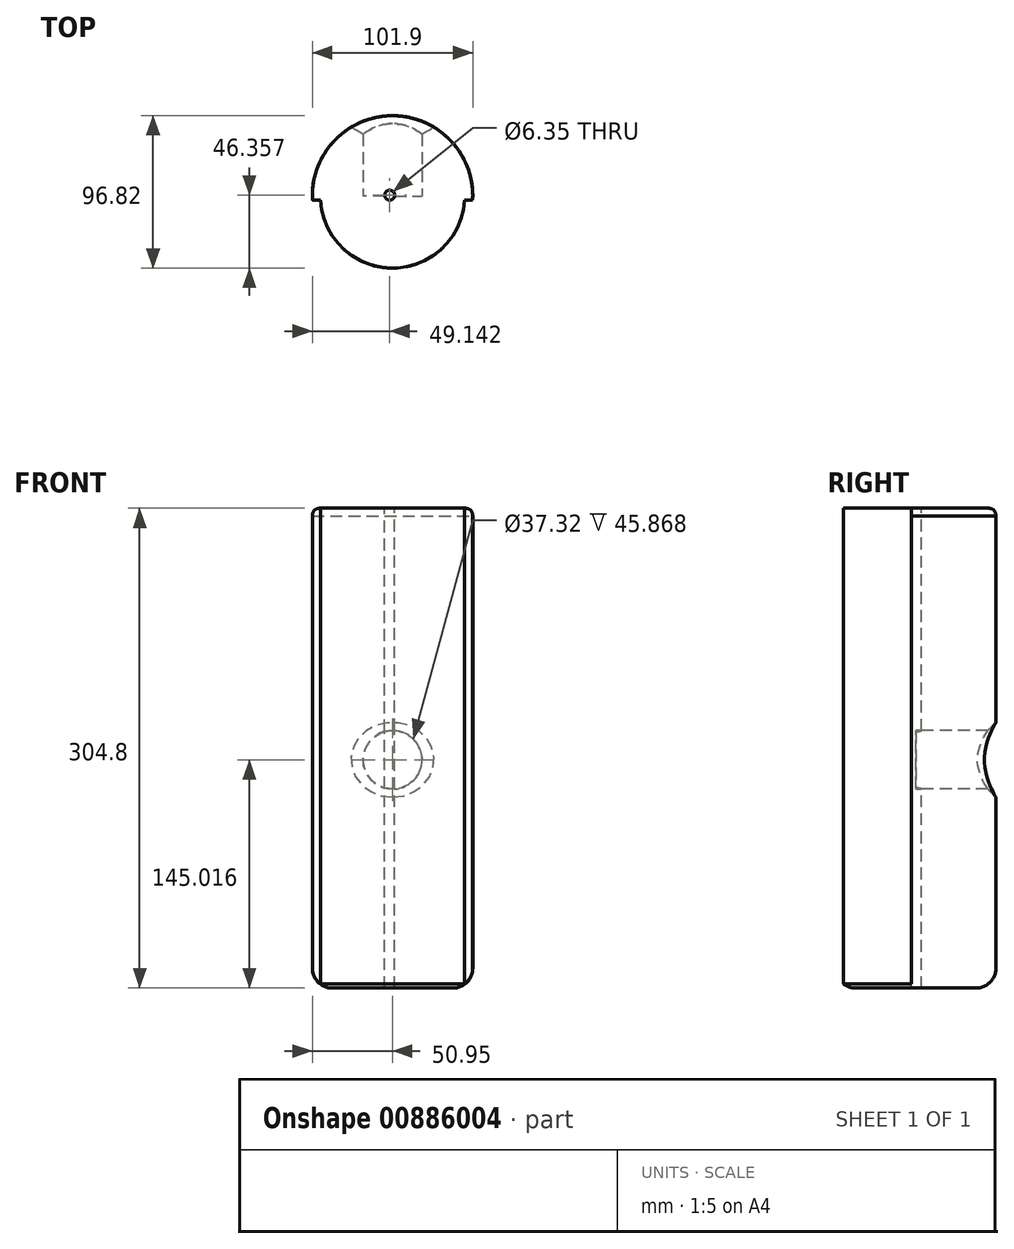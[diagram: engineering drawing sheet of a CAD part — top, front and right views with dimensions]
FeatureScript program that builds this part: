
annotation { "Feature Type Name" : "Feature", "Feature Type Description" : "" }
export const myFeature = defineFeature(function(context is Context, id is Id, definition is map)
    precondition{}
    {
        {
            var Q0;
            Q0=qCreatedBy(makeId("Top.planeOp"),FACE);
            var sketch = newSketch(context, id + "F0", { "sketchPlane" : qUnion([Q0])});
            skCircle(sketch, "E0", {"center": v(0, 0) * mm, "radius": 50.95 * mm});
            skSolve(sketch);
        }
        {
            var Q0;
            Q0 = qSketchRegion(id + "F0", true);
            extrude(context, id + "F1", {"entities" : qUnion([Q0]), "depth" : 304.8 * mm, "offsetDistance" : 25.4 * mm});
        }
        {
            var Q0;
            Q0=qCreatedBy(makeId("Front.planeOp"),FACE);
            var sketch = newSketch(context, id + "F2", { "sketchPlane" : qUnion([Q0])});
            skCircle(sketch, "E1", {"center": v(0, 145.02) * mm, "radius": 18.66 * mm});
            skSolve(sketch);
        }
        {
            var Q0;
            Q0 = qSketchRegion(id + "F2", true);
            extrude(context, id + "F3", {"entities" : qUnion([Q0]), "operationType" : NewBodyOperationType.REMOVE, "endBound" : BoundingType.THROUGH_ALL, "oppositeDirection" : true, "depth" : 25.4 * mm, "offsetDistance" : 25.4 * mm});
        }
        {
            var Q0;
            Q0=makeQuery(id+"F1.opExtrude","CAP_EDGE",EDGE,{"disambiguationData":[OSD([sQuery(id+"F0.wireOp",EDGE,"E0")])],"isStart":true});
            fillet(context, id + "F4", {"entities" : qUnion([Q0]), "radius" : 12.7 * mm, "tangentPropagation" : true, "allowEdgeOverflow" : false});
        }
        {
            var Q0;
            Q0=makeQuery(id+"F3.boolean.opBoolean","INTERSECT",EDGE,{"derivedFrom":[makeQuery(id+"F1.opExtrude","SWEPT_FACE",FACE,{"disambiguationData":[OSD([sQuery(id+"F0.wireOp",EDGE,"E0")])]}),makeQuery(id+"F3.opExtrude","SWEPT_FACE",FACE,{"disambiguationData":[OSD([sQuery(id+"F2.wireOp",EDGE,"E1")])]})]});
            chamfer(context, id + "F5", {"entities" : qUnion([Q0]), "width" : 5.08 * mm, "tangentPropagation" : true});
        }
        {
            var Q0;
            Q0=makeQuery(id+"F1.opExtrude","CAP_EDGE",EDGE,{"disambiguationData":[OSD([sQuery(id+"F0.wireOp",EDGE,"E0")])],"isStart":false});
            fillet(context, id + "F6", {"entities" : qUnion([Q0]), "tangentPropagation" : true, "crossSection" : FilletCrossSection.CURVATURE, "radius" : 5.08 * mm, "magnitude" : 0.5, "defaultsChanged" : false, "vertexSettings" : []});
        }
        {
            var Q0;
            Q0=makeQuery(id+"F1.opExtrude","CAP_FACE",FACE,{"disambiguationData":[OSD([sQuery(id+"F0.wireOp",EDGE,"E0")])],"isStart":false});
            var sketch = newSketch(context, id + "F7", { "sketchPlane" : qUnion([Q0])});
            skLineSegment(sketch, "E2.bottom", {"start": v(-96.32, -2.57) * mm, "end": v(89.81, -2.57) * mm});
            skLineSegment(sketch, "E2.top", {"start": v(-96.32, -75.73) * mm, "end": v(89.81, -75.73) * mm});
            skLineSegment(sketch, "E2.left", {"start": v(-96.32, -2.57) * mm, "end": v(-96.32, -75.73) * mm});
            skLineSegment(sketch, "E2.right", {"start": v(89.81, -2.57) * mm, "end": v(89.81, -75.73) * mm});
            skSolve(sketch);
        }
        {
            var Q0;
            Q0=makeQuery(id+"F7.imprint","IMPRINT",FACE,{"disambiguationData":[TD([[makeQuery(id+"F7.imprint","IMPRINT",EDGE,{"derivedFrom":sQuery(id+"F7.wireOp",EDGE,"E2.top")}),1.0]])]});
            extrude(context, id + "F8", {"entities" : qUnion([Q0]), "operationType" : NewBodyOperationType.REMOVE, "endBound" : BoundingType.THROUGH_ALL, "oppositeDirection" : true, "depth" : 25.4 * mm, "offsetDistance" : 25.4 * mm});
        }
        {
            var Q0;
            Q0=makeQuery(id+"F1.opExtrude","CAP_FACE",FACE,{"disambiguationData":[OSD([sQuery(id+"F0.wireOp",EDGE,"E0")])],"isStart":false});
            var sketch = newSketch(context, id + "F9", { "sketchPlane" : qUnion([Q0])});
            skCircle(sketch, "E3", {"center": v(-1.8, 0.49) * mm, "radius": 17.62 * mm});
            skSolve(sketch);
        }
        {
            var Q0;
            Q0=sQuery(id+"F9.wireOp",VERTEX,"E3.center");
            var Q1;
            Q1=makeQuery(id+"F1.opExtrude","SWEPT_BODY",BODY,{"disambiguationData":[OSD([sQuery(id+"F0.wireOp",EDGE,"E0")])]});
            hole(context, id + "F10", {"style" : HoleStyle.SIMPLE, "endStyle" : HoleEndStyle.THROUGH, "holeDiameter" : 6.35 * mm, "majorDiameter" : 6.35 * mm, "isTappedThrough" : true, "tappedDepth" : 12.7 * mm, "tapClearance" : 3, "locations" : qUnion([Q0]), "scope" : qUnion([Q1])});
        }
    });
